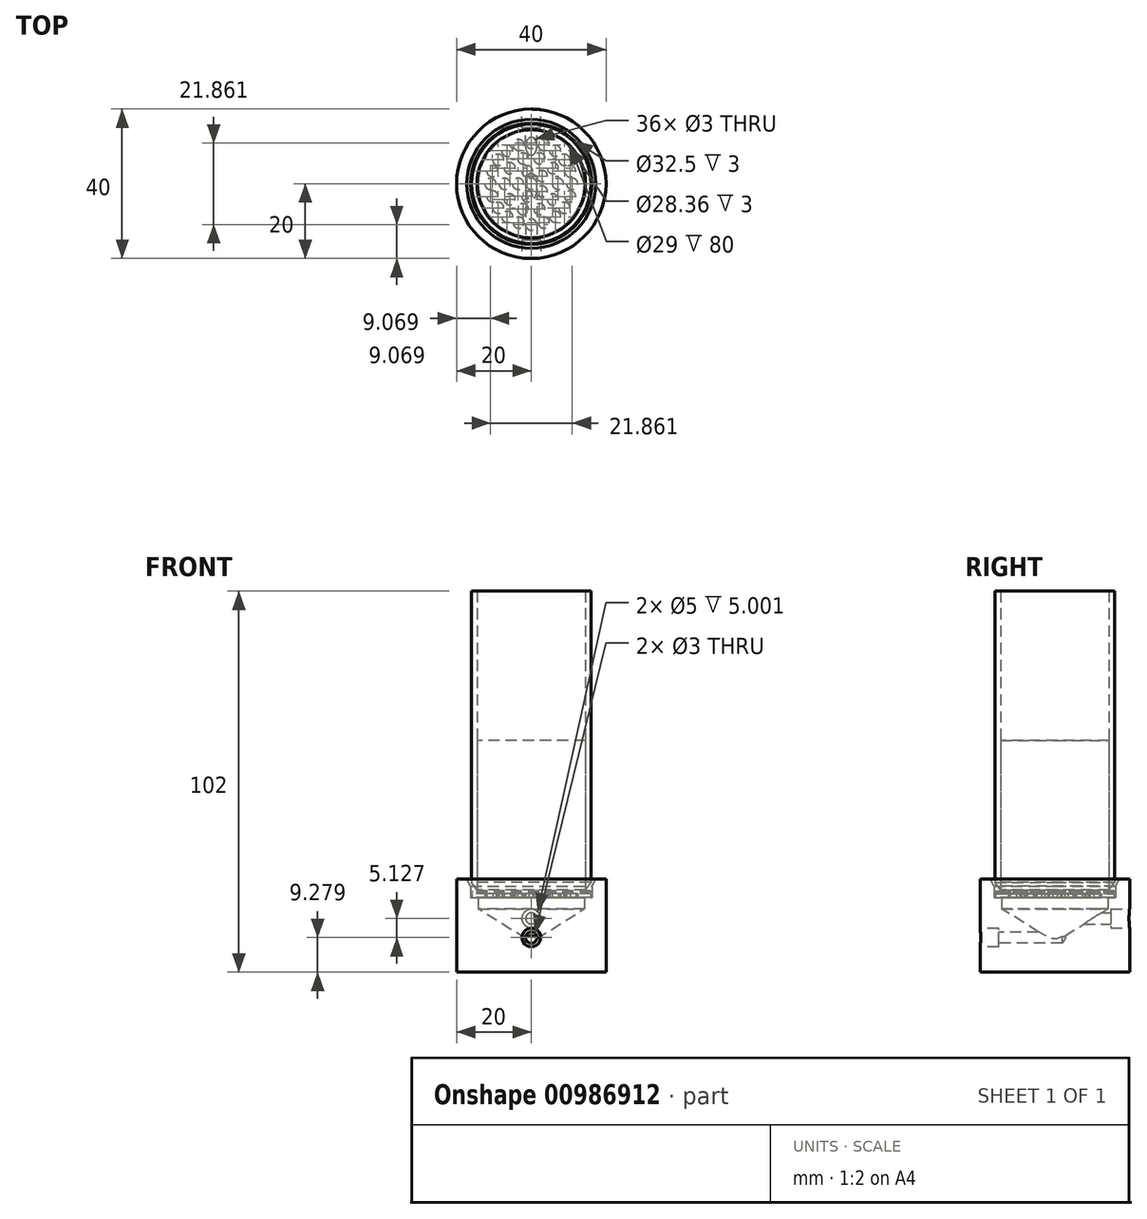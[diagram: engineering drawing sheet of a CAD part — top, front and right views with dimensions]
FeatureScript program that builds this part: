
annotation { "Feature Type Name" : "Feature", "Feature Type Description" : "" }
export const myFeature = defineFeature(function(context is Context, id is Id, definition is map)
    precondition{}
    {
        {
            var Q0;
            Q0=qCreatedBy(makeId("Top.planeOp"),FACE);
            var sketch = newSketch(context, id + "F0", { "sketchPlane" : qUnion([Q0])});
            skCircle(sketch, "E0", {"center": v(0, 0) * mm, "radius": 16 * mm});
            skCircle(sketch, "E1", {"center": v(0, 0) * mm, "radius": 14.5 * mm});
            skSolve(sketch);
        }
        {
            var Q0;
            Q0=makeQuery(id+"F0.imprint","IMPRINT",FACE,{"disambiguationData":[TD([[makeQuery(id+"F0.imprint","IMPRINT",EDGE,{"derivedFrom":sQuery(id+"F0.wireOp",EDGE,"E0")}),1.0]])]});
            extrude(context, id + "F1", {"entities" : qUnion([Q0]), "depth" : 80 * mm, "offsetDistance" : 25 * mm});
        }
        {
            var Q0;
            Q0=qCreatedBy(makeId("Front.planeOp"),FACE);
            var sketch = newSketch(context, id + "F2", { "sketchPlane" : qUnion([Q0])});
            skLineSegment(sketch, "E2", {"start": v(-16.25, 0) * mm, "end": v(-16.25, 5) * mm});
            skLineSegment(sketch, "E3", {"start": v(-16.25, 5) * mm, "end": v(-20, 5) * mm});
            skLineSegment(sketch, "E4", {"start": v(-20, 5) * mm, "end": v(-20, -20) * mm});
            skLineSegment(sketch, "E5", {"start": v(-20, -20) * mm, "end": v(0, -20) * mm});
            skLineSegment(sketch, "E6", {"start": v(0, -20) * mm, "end": v(0, -12) * mm});
            skLineSegment(sketch, "E7", {"start": v(0, -12) * mm, "end": v(-14.18, -3) * mm});
            skLineSegment(sketch, "E8", {"start": v(-14.18, -3) * mm, "end": v(-14.18, 0) * mm});
            skLineSegment(sketch, "E9", {"start": v(-14.18, 0) * mm, "end": v(-16.25, 0) * mm});
            skSolve(sketch);
        }
        {
            var Q0;
            Q0=makeQuery(id+"F2.imprint","IMPRINT",FACE,{"disambiguationData":[TD([[makeQuery(id+"F2.imprint","IMPRINT",EDGE,{"derivedFrom":sQuery(id+"F2.wireOp",EDGE,"E2")}),1.0]])]});
            var Q1;
            Q1=sQuery(id+"F2.wireOp",EDGE,"E6");
            revolve(context, id + "F3", {"surfaceOperationType" : NewSurfaceOperationType.NEW, "entities" : qUnion([Q0]), "axis" : qUnion([Q1]), "revolveType" : RevolveType.FULL});
        }
        {
            var Q0;
            Q0=qCreatedBy(makeId("Front.planeOp"),FACE);
            cPlane(context, id + "F4", {"entities" : qUnion([Q0]), "cplaneType" : CPlaneType.OFFSET, "offset" : 20 * mm, "width" : 150 * mm, "height" : 150 * mm});
        }
        {
            var Q0;
            Q0=qCreatedBy(id+"F4.planeOp",FACE);
            var sketch = newSketch(context, id + "F5", { "sketchPlane" : qUnion([Q0])});
            skLineSegment(sketch, "E10", {"start": v(0, -20.72) * mm, "end": v(0, -10.72) * mm});
            skSolve(sketch);
        }
        {
            var Q0;
            Q0=sQuery(id+"F5.wireOp",VERTEX,"E10.end");
            var Q1;
            Q1=makeQuery(id+"F3.opRevolve","SWEPT_BODY",BODY,{"disambiguationData":[OSD([sQuery(id+"F2.wireOp",EDGE,"E2"),sQuery(id+"F2.wireOp",EDGE,"E3"),sQuery(id+"F2.wireOp",EDGE,"E4"),sQuery(id+"F2.wireOp",EDGE,"E5"),sQuery(id+"F2.wireOp",EDGE,"E6"),sQuery(id+"F2.wireOp",EDGE,"E7"),sQuery(id+"F2.wireOp",EDGE,"E8"),sQuery(id+"F2.wireOp",EDGE,"E9")])]});
            hole(context, id + "F6", {"style" : HoleStyle.C_BORE, "endStyle" : HoleEndStyle.BLIND, "holeDiameter" : 3 * mm, "cBoreDiameter" : 5 * mm, "cBoreDepth" : 5 * mm, "majorDiameter" : 5 * mm, "holeDepth" : 22 * mm, "isTappedThrough" : true, "tappedDepth" : 12 * mm, "tapClearance" : 3, "startFromSketch" : true, "locations" : qUnion([Q0]), "scope" : qUnion([Q1])});
        }
        {
            var Q0;
            Q0=qCreatedBy(makeId("Front.planeOp"),FACE);
            cPlane(context, id + "F7", {"entities" : qUnion([Q0]), "cplaneType" : CPlaneType.OFFSET, "offset" : 20 * mm, "oppositeDirection" : true, "width" : 150 * mm, "height" : 150 * mm});
        }
        {
            var Q0;
            Q0=qCreatedBy(id+"F7.planeOp",FACE);
            var sketch = newSketch(context, id + "F8", { "sketchPlane" : qUnion([Q0])});
            skLineSegment(sketch, "E11", {"start": v(0, -19.77) * mm, "end": v(0, -5.6) * mm});
            skSolve(sketch);
        }
        {
            var Q0;
            Q0=sQuery(id+"F8.wireOp",VERTEX,"E11.end");
            var Q1;
            Q1=makeQuery(id+"F3.opRevolve","SWEPT_BODY",BODY,{"disambiguationData":[OSD([sQuery(id+"F2.wireOp",EDGE,"E2"),sQuery(id+"F2.wireOp",EDGE,"E3"),sQuery(id+"F2.wireOp",EDGE,"E4"),sQuery(id+"F2.wireOp",EDGE,"E5"),sQuery(id+"F2.wireOp",EDGE,"E6"),sQuery(id+"F2.wireOp",EDGE,"E7"),sQuery(id+"F2.wireOp",EDGE,"E8"),sQuery(id+"F2.wireOp",EDGE,"E9")])]});
            hole(context, id + "F9", {"style" : HoleStyle.C_BORE, "endStyle" : HoleEndStyle.BLIND, "oppositeDirection" : true, "holeDiameter" : 3 * mm, "cBoreDiameter" : 5 * mm, "cBoreDepth" : 5 * mm, "majorDiameter" : 5 * mm, "holeDepth" : 22 * mm, "isTappedThrough" : true, "tappedDepth" : 12 * mm, "tapClearance" : 3, "startFromSketch" : true, "locations" : qUnion([Q0]), "scope" : qUnion([Q1])});
        }
        {
            var Q0;
            Q0=makeQuery(id+"F1.opExtrude","SWEPT_BODY",BODY,{"disambiguationData":[OSD([sQuery(id+"F0.wireOp",EDGE,"E0"),sQuery(id+"F0.wireOp",EDGE,"E1")])]});
            transform(context, id + "F10", {"entities" : qUnion([Q0]), "transformType" : TransformType.TRANSLATION_3D, "dx" : 0 * mm, "dy" : 0 * mm, "dz" : 2 * mm, "makeCopy" : false});
        }
        {
            var Q0;
            Q0=qCreatedBy(makeId("Top.planeOp"),FACE);
            var sketch = newSketch(context, id + "F11", { "sketchPlane" : qUnion([Q0])});
            skCircle(sketch, "E12", {"center": v(0, 0) * mm, "radius": 15.9 * mm});
            skSolve(sketch);
        }
        {
            var Q0;
            Q0=makeQuery(id+"F11.imprint","IMPRINT",FACE,{"disambiguationData":[TD([[makeQuery(id+"F11.imprint","IMPRINT",EDGE,{"derivedFrom":sQuery(id+"F11.wireOp",EDGE,"E12")}),1.0]])]});
            extrude(context, id + "F12", {"entities" : qUnion([Q0]), "depth" : 1 * mm, "offsetDistance" : 25 * mm});
        }
        {
            var Q0;
            Q0=qCreatedBy(makeId("Top.planeOp"),FACE);
            var sketch = newSketch(context, id + "F13", { "sketchPlane" : qUnion([Q0])});
            skCircle(sketch, "E13", {"center": v(0, 0) * mm, "radius": 1.5 * mm});
            skCircle(sketch, "E14", {"center": v(-3.54, 0) * mm, "radius": 1.5 * mm});
            skCircle(sketch, "E15.1.0", {"center": v(-1.1, -3.36) * mm, "radius": 1.5 * mm});
            skCircle(sketch, "E15.2.0", {"center": v(2.86, -2.08) * mm, "radius": 1.5 * mm});
            skCircle(sketch, "E15.3.0", {"center": v(2.86, 2.08) * mm, "radius": 1.5 * mm});
            skCircle(sketch, "E15.4.0", {"center": v(-1.1, 3.36) * mm, "radius": 1.5 * mm});
            skCircle(sketch, "E16", {"center": v(-7.13, 0) * mm, "radius": 1.5 * mm});
            skCircle(sketch, "E17.1.0", {"center": v(-5.77, -4.19) * mm, "radius": 1.5 * mm});
            skCircle(sketch, "E17.2.0", {"center": v(-2.2, -6.78) * mm, "radius": 1.5 * mm});
            skCircle(sketch, "E17.3.0", {"center": v(2.2, -6.78) * mm, "radius": 1.5 * mm});
            skCircle(sketch, "E17.4.0", {"center": v(5.77, -4.19) * mm, "radius": 1.5 * mm});
            skCircle(sketch, "E17.5.0", {"center": v(7.13, 0) * mm, "radius": 1.5 * mm});
            skCircle(sketch, "E17.6.0", {"center": v(5.77, 4.19) * mm, "radius": 1.5 * mm});
            skCircle(sketch, "E17.7.0", {"center": v(2.2, 6.78) * mm, "radius": 1.5 * mm});
            skCircle(sketch, "E17.8.0", {"center": v(-2.2, 6.78) * mm, "radius": 1.5 * mm});
            skCircle(sketch, "E17.9.0", {"center": v(-5.77, 4.19) * mm, "radius": 1.5 * mm});
            skCircle(sketch, "E18", {"center": v(-10.93, 0) * mm, "radius": 1.5 * mm});
            skCircle(sketch, "E19.1.0", {"center": v(-10.4, -3.38) * mm, "radius": 1.5 * mm});
            skCircle(sketch, "E19.2.0", {"center": v(-8.84, -6.42) * mm, "radius": 1.5 * mm});
            skCircle(sketch, "E19.3.0", {"center": v(-6.42, -8.84) * mm, "radius": 1.5 * mm});
            skCircle(sketch, "E19.4.0", {"center": v(-3.38, -10.4) * mm, "radius": 1.5 * mm});
            skCircle(sketch, "E19.5.0", {"center": v(0, -10.93) * mm, "radius": 1.5 * mm});
            skCircle(sketch, "E19.6.0", {"center": v(3.38, -10.4) * mm, "radius": 1.5 * mm});
            skCircle(sketch, "E19.7.0", {"center": v(6.42, -8.84) * mm, "radius": 1.5 * mm});
            skCircle(sketch, "E19.8.0", {"center": v(8.84, -6.42) * mm, "radius": 1.5 * mm});
            skCircle(sketch, "E19.9.0", {"center": v(10.4, -3.38) * mm, "radius": 1.5 * mm});
            skCircle(sketch, "E19.10.0", {"center": v(10.93, 0) * mm, "radius": 1.5 * mm});
            skCircle(sketch, "E19.11.0", {"center": v(10.4, 3.38) * mm, "radius": 1.5 * mm});
            skCircle(sketch, "E19.12.0", {"center": v(8.84, 6.42) * mm, "radius": 1.5 * mm});
            skCircle(sketch, "E19.13.0", {"center": v(6.42, 8.84) * mm, "radius": 1.5 * mm});
            skCircle(sketch, "E19.14.0", {"center": v(3.38, 10.4) * mm, "radius": 1.5 * mm});
            skCircle(sketch, "E19.15.0", {"center": v(0, 10.93) * mm, "radius": 1.5 * mm});
            skCircle(sketch, "E19.16.0", {"center": v(-3.38, 10.4) * mm, "radius": 1.5 * mm});
            skCircle(sketch, "E19.17.0", {"center": v(-6.42, 8.84) * mm, "radius": 1.5 * mm});
            skCircle(sketch, "E19.18.0", {"center": v(-8.84, 6.42) * mm, "radius": 1.5 * mm});
            skCircle(sketch, "E19.19.0", {"center": v(-10.4, 3.38) * mm, "radius": 1.5 * mm});
            skSolve(sketch);
        }
        {
            var Q0;
            Q0=makeQuery(id+"F13.imprint","IMPRINT",FACE,{"disambiguationData":[TD([[makeQuery(id+"F13.imprint","IMPRINT",EDGE,{"derivedFrom":sQuery(id+"F13.wireOp",EDGE,"E19.7.0")}),1.0]])]});
            var Q1;
            Q1=makeQuery(id+"F13.imprint","IMPRINT",FACE,{"disambiguationData":[TD([[makeQuery(id+"F13.imprint","IMPRINT",EDGE,{"derivedFrom":sQuery(id+"F13.wireOp",EDGE,"E19.3.0")}),1.0]])]});
            var Q2;
            Q2=makeQuery(id+"F13.imprint","IMPRINT",FACE,{"disambiguationData":[TD([[makeQuery(id+"F13.imprint","IMPRINT",EDGE,{"derivedFrom":sQuery(id+"F13.wireOp",EDGE,"E19.1.0")}),1.0]])]});
            var Q3;
            Q3=makeQuery(id+"F13.imprint","IMPRINT",FACE,{"disambiguationData":[TD([[makeQuery(id+"F13.imprint","IMPRINT",EDGE,{"derivedFrom":sQuery(id+"F13.wireOp",EDGE,"E19.5.0")}),1.0]])]});
            var Q4;
            Q4=makeQuery(id+"F13.imprint","IMPRINT",FACE,{"disambiguationData":[TD([[makeQuery(id+"F13.imprint","IMPRINT",EDGE,{"derivedFrom":sQuery(id+"F13.wireOp",EDGE,"E19.17.0")}),1.0]])]});
            var Q5;
            Q5=makeQuery(id+"F13.imprint","IMPRINT",FACE,{"disambiguationData":[TD([[makeQuery(id+"F13.imprint","IMPRINT",EDGE,{"derivedFrom":sQuery(id+"F13.wireOp",EDGE,"E19.14.0")}),1.0]])]});
            var Q6;
            Q6=makeQuery(id+"F13.imprint","IMPRINT",FACE,{"disambiguationData":[TD([[makeQuery(id+"F13.imprint","IMPRINT",EDGE,{"derivedFrom":sQuery(id+"F13.wireOp",EDGE,"E19.19.0")}),1.0]])]});
            var Q7;
            Q7=makeQuery(id+"F13.imprint","IMPRINT",FACE,{"disambiguationData":[TD([[makeQuery(id+"F13.imprint","IMPRINT",EDGE,{"derivedFrom":sQuery(id+"F13.wireOp",EDGE,"E19.15.0")}),1.0]])]});
            var Q8;
            Q8=makeQuery(id+"F13.imprint","IMPRINT",FACE,{"disambiguationData":[TD([[makeQuery(id+"F13.imprint","IMPRINT",EDGE,{"derivedFrom":sQuery(id+"F13.wireOp",EDGE,"E17.9.0")}),1.0]])]});
            var Q9;
            Q9=makeQuery(id+"F13.imprint","IMPRINT",FACE,{"disambiguationData":[TD([[makeQuery(id+"F13.imprint","IMPRINT",EDGE,{"derivedFrom":sQuery(id+"F13.wireOp",EDGE,"E15.3.0")}),1.0]])]});
            var Q10;
            Q10=makeQuery(id+"F13.imprint","IMPRINT",FACE,{"disambiguationData":[TD([[makeQuery(id+"F13.imprint","IMPRINT",EDGE,{"derivedFrom":sQuery(id+"F13.wireOp",EDGE,"E17.1.0")}),1.0]])]});
            var Q11;
            Q11=makeQuery(id+"F13.imprint","IMPRINT",FACE,{"disambiguationData":[TD([[makeQuery(id+"F13.imprint","IMPRINT",EDGE,{"derivedFrom":sQuery(id+"F13.wireOp",EDGE,"E19.16.0")}),1.0]])]});
            var Q12;
            Q12=makeQuery(id+"F13.imprint","IMPRINT",FACE,{"disambiguationData":[TD([[makeQuery(id+"F13.imprint","IMPRINT",EDGE,{"derivedFrom":sQuery(id+"F13.wireOp",EDGE,"E19.8.0")}),1.0]])]});
            var Q13;
            Q13=makeQuery(id+"F13.imprint","IMPRINT",FACE,{"disambiguationData":[TD([[makeQuery(id+"F13.imprint","IMPRINT",EDGE,{"derivedFrom":sQuery(id+"F13.wireOp",EDGE,"E14")}),1.0]])]});
            var Q14;
            Q14=makeQuery(id+"F13.imprint","IMPRINT",FACE,{"disambiguationData":[TD([[makeQuery(id+"F13.imprint","IMPRINT",EDGE,{"derivedFrom":sQuery(id+"F13.wireOp",EDGE,"E17.2.0")}),1.0]])]});
            var Q15;
            Q15=makeQuery(id+"F13.imprint","IMPRINT",FACE,{"disambiguationData":[TD([[makeQuery(id+"F13.imprint","IMPRINT",EDGE,{"derivedFrom":sQuery(id+"F13.wireOp",EDGE,"E17.8.0")}),1.0]])]});
            var Q16;
            Q16=makeQuery(id+"F13.imprint","IMPRINT",FACE,{"disambiguationData":[TD([[makeQuery(id+"F13.imprint","IMPRINT",EDGE,{"derivedFrom":sQuery(id+"F13.wireOp",EDGE,"E19.12.0")}),1.0]])]});
            var Q17;
            Q17=makeQuery(id+"F13.imprint","IMPRINT",FACE,{"disambiguationData":[TD([[makeQuery(id+"F13.imprint","IMPRINT",EDGE,{"derivedFrom":sQuery(id+"F13.wireOp",EDGE,"E17.7.0")}),1.0]])]});
            var Q18;
            Q18=makeQuery(id+"F13.imprint","IMPRINT",FACE,{"disambiguationData":[TD([[makeQuery(id+"F13.imprint","IMPRINT",EDGE,{"derivedFrom":sQuery(id+"F13.wireOp",EDGE,"E19.13.0")}),1.0]])]});
            var Q19;
            Q19=makeQuery(id+"F13.imprint","IMPRINT",FACE,{"disambiguationData":[TD([[makeQuery(id+"F13.imprint","IMPRINT",EDGE,{"derivedFrom":sQuery(id+"F13.wireOp",EDGE,"E13")}),1.0]])]});
            var Q20;
            Q20=makeQuery(id+"F13.imprint","IMPRINT",FACE,{"disambiguationData":[TD([[makeQuery(id+"F13.imprint","IMPRINT",EDGE,{"derivedFrom":sQuery(id+"F13.wireOp",EDGE,"E19.9.0")}),1.0]])]});
            var Q21;
            Q21=makeQuery(id+"F13.imprint","IMPRINT",FACE,{"disambiguationData":[TD([[makeQuery(id+"F13.imprint","IMPRINT",EDGE,{"derivedFrom":sQuery(id+"F13.wireOp",EDGE,"E19.10.0")}),1.0]])]});
            var Q22;
            Q22=makeQuery(id+"F13.imprint","IMPRINT",FACE,{"disambiguationData":[TD([[makeQuery(id+"F13.imprint","IMPRINT",EDGE,{"derivedFrom":sQuery(id+"F13.wireOp",EDGE,"E17.6.0")}),1.0]])]});
            var Q23;
            Q23=makeQuery(id+"F13.imprint","IMPRINT",FACE,{"disambiguationData":[TD([[makeQuery(id+"F13.imprint","IMPRINT",EDGE,{"derivedFrom":sQuery(id+"F13.wireOp",EDGE,"E17.4.0")}),1.0]])]});
            var Q24;
            Q24=makeQuery(id+"F13.imprint","IMPRINT",FACE,{"disambiguationData":[TD([[makeQuery(id+"F13.imprint","IMPRINT",EDGE,{"derivedFrom":sQuery(id+"F13.wireOp",EDGE,"E19.11.0")}),1.0]])]});
            var Q25;
            Q25=makeQuery(id+"F13.imprint","IMPRINT",FACE,{"disambiguationData":[TD([[makeQuery(id+"F13.imprint","IMPRINT",EDGE,{"derivedFrom":sQuery(id+"F13.wireOp",EDGE,"E17.3.0")}),1.0]])]});
            var Q26;
            Q26=makeQuery(id+"F13.imprint","IMPRINT",FACE,{"disambiguationData":[TD([[makeQuery(id+"F13.imprint","IMPRINT",EDGE,{"derivedFrom":sQuery(id+"F13.wireOp",EDGE,"E16")}),1.0]])]});
            var Q27;
            Q27=makeQuery(id+"F13.imprint","IMPRINT",FACE,{"disambiguationData":[TD([[makeQuery(id+"F13.imprint","IMPRINT",EDGE,{"derivedFrom":sQuery(id+"F13.wireOp",EDGE,"E15.1.0")}),1.0]])]});
            var Q28;
            Q28=makeQuery(id+"F13.imprint","IMPRINT",FACE,{"disambiguationData":[TD([[makeQuery(id+"F13.imprint","IMPRINT",EDGE,{"derivedFrom":sQuery(id+"F13.wireOp",EDGE,"E19.6.0")}),1.0]])]});
            var Q29;
            Q29=makeQuery(id+"F13.imprint","IMPRINT",FACE,{"disambiguationData":[TD([[makeQuery(id+"F13.imprint","IMPRINT",EDGE,{"derivedFrom":sQuery(id+"F13.wireOp",EDGE,"E15.2.0")}),1.0]])]});
            var Q30;
            Q30=makeQuery(id+"F13.imprint","IMPRINT",FACE,{"disambiguationData":[TD([[makeQuery(id+"F13.imprint","IMPRINT",EDGE,{"derivedFrom":sQuery(id+"F13.wireOp",EDGE,"E15.4.0")}),1.0]])]});
            var Q31;
            Q31=makeQuery(id+"F13.imprint","IMPRINT",FACE,{"disambiguationData":[TD([[makeQuery(id+"F13.imprint","IMPRINT",EDGE,{"derivedFrom":sQuery(id+"F13.wireOp",EDGE,"E19.4.0")}),1.0]])]});
            var Q32;
            Q32=makeQuery(id+"F13.imprint","IMPRINT",FACE,{"disambiguationData":[TD([[makeQuery(id+"F13.imprint","IMPRINT",EDGE,{"derivedFrom":sQuery(id+"F13.wireOp",EDGE,"E19.2.0")}),1.0]])]});
            var Q33;
            Q33=makeQuery(id+"F13.imprint","IMPRINT",FACE,{"disambiguationData":[TD([[makeQuery(id+"F13.imprint","IMPRINT",EDGE,{"derivedFrom":sQuery(id+"F13.wireOp",EDGE,"E18")}),1.0]])]});
            var Q34;
            Q34=makeQuery(id+"F13.imprint","IMPRINT",FACE,{"disambiguationData":[TD([[makeQuery(id+"F13.imprint","IMPRINT",EDGE,{"derivedFrom":sQuery(id+"F13.wireOp",EDGE,"E19.18.0")}),1.0]])]});
            var Q35;
            Q35=makeQuery(id+"F13.imprint","IMPRINT",FACE,{"disambiguationData":[TD([[makeQuery(id+"F13.imprint","IMPRINT",EDGE,{"derivedFrom":sQuery(id+"F13.wireOp",EDGE,"E17.5.0")}),1.0]])]});
            extrude(context, id + "F14", {"entities" : qUnion([Q0, Q1, Q2, Q3, Q4, Q5, Q6, Q7, Q8, Q9, Q10, Q11, Q12, Q13, Q14, Q15, Q16, Q17, Q18, Q19, Q20, Q21, Q22, Q23, Q24, Q25, Q26, Q27, Q28, Q29, Q30, Q31, Q32, Q33, Q34, Q35]), "operationType" : NewBodyOperationType.REMOVE, "depth" : 1 * mm, "offsetDistance" : 25 * mm});
        }
        {
            var Q0;
            Q0=qCreatedBy(makeId("Top.planeOp"),FACE);
            var sketch = newSketch(context, id + "F15", { "sketchPlane" : qUnion([Q0])});
            skCircle(sketch, "E20", {"center": v(0, 0) * mm, "radius": 14.5 * mm});
            skSolve(sketch);
        }
        {
            var Q0;
            Q0=makeQuery(id+"F15.imprint","IMPRINT",FACE,{"disambiguationData":[TD([[makeQuery(id+"F15.imprint","IMPRINT",EDGE,{"derivedFrom":sQuery(id+"F15.wireOp",EDGE,"E20")}),1.0]])]});
            extrude(context, id + "F16", {"entities" : qUnion([Q0]), "depth" : 40 * mm, "offsetDistance" : 25 * mm});
        }
        {
            var Q0;
            Q0=makeQuery(id+"F16.opExtrude","SWEPT_BODY",BODY,{"disambiguationData":[OSD([sQuery(id+"F15.wireOp",EDGE,"E20")])]});
            transform(context, id + "F17", {"entities" : qUnion([Q0]), "transformType" : TransformType.TRANSLATION_3D, "dx" : 0 * mm, "dy" : 0 * mm, "dz" : 2 * mm, "makeCopy" : false});
        }
        {
            var Q0;
            Q0=qCreatedBy(makeId("Top.planeOp"),FACE);
            var sketch = newSketch(context, id + "F18", { "sketchPlane" : qUnion([Q0])});
            skCircle(sketch, "E21", {"center": v(0, 0) * mm, "radius": 15.9 * mm});
            skSolve(sketch);
        }
        {
            var Q0;
            Q0=makeQuery(id+"F18.imprint","IMPRINT",FACE,{"disambiguationData":[TD([[makeQuery(id+"F18.imprint","IMPRINT",EDGE,{"derivedFrom":sQuery(id+"F18.wireOp",EDGE,"E21")}),1.0]])]});
            extrude(context, id + "F19", {"entities" : qUnion([Q0]), "depth" : 0.5 * mm, "offsetDistance" : 25 * mm});
        }
        {
            var Q0;
            Q0=makeQuery(id+"F19.opExtrude","SWEPT_BODY",BODY,{"disambiguationData":[OSD([sQuery(id+"F18.wireOp",EDGE,"E21")])]});
            transform(context, id + "F20", {"entities" : qUnion([Q0]), "transformType" : TransformType.TRANSLATION_3D, "dx" : 0 * mm, "dy" : 0 * mm, "dz" : 1.25 * mm, "makeCopy" : false});
        }
        {
            var Q0;
            Q0=makeQuery(id+"F3.opRevolve","SWEPT_EDGE",EDGE,{"disambiguationData":[OSD([sQuery(id+"F2.wireOp",EDGE,"E2"),sQuery(id+"F2.wireOp",EDGE,"E3")])]});
            chamfer(context, id + "F21", {"entities" : qUnion([Q0]), "chamferType" : ChamferType.TWO_OFFSETS, "width1" : 1 * mm, "oppositeDirection" : false, "width2" : 2 * mm, "tangentPropagation" : true});
        }
        {
            var Q0;
            Q0=makeQuery(id+"F1.opExtrude","CAP_EDGE",EDGE,{"disambiguationData":[OSD([sQuery(id+"F0.wireOp",EDGE,"E0")])],"isStart":true});
            chamfer(context, id + "F22", {"entities" : qUnion([Q0]), "chamferType" : ChamferType.TWO_OFFSETS, "width1" : 2 * mm, "oppositeDirection" : false, "width2" : 1.5 * mm, "tangentPropagation" : true});
        }
        {
            var Q0;
            Q0=makeQuery(id+"F3.opRevolve","SWEPT_BODY",BODY,{"disambiguationData":[OSD([sQuery(id+"F2.wireOp",EDGE,"E2"),sQuery(id+"F2.wireOp",EDGE,"E3"),sQuery(id+"F2.wireOp",EDGE,"E4"),sQuery(id+"F2.wireOp",EDGE,"E5"),sQuery(id+"F2.wireOp",EDGE,"E6"),sQuery(id+"F2.wireOp",EDGE,"E7"),sQuery(id+"F2.wireOp",EDGE,"E8"),sQuery(id+"F2.wireOp",EDGE,"E9")])]});
            transform(context, id + "F23", {"entities" : qUnion([Q0]), "transformType" : TransformType.TRANSLATION_3D, "dx" : 0 * mm, "dy" : 0 * mm, "dz" : 0 * mm, "makeCopy" : true});
        }
        {
            var Q0;
            Q0=makeQuery(id+"F3.opRevolve","SWEPT_BODY",BODY,{"disambiguationData":[OSD([sQuery(id+"F2.wireOp",EDGE,"E2"),sQuery(id+"F2.wireOp",EDGE,"E3"),sQuery(id+"F2.wireOp",EDGE,"E4"),sQuery(id+"F2.wireOp",EDGE,"E5"),sQuery(id+"F2.wireOp",EDGE,"E6"),sQuery(id+"F2.wireOp",EDGE,"E7"),sQuery(id+"F2.wireOp",EDGE,"E8"),sQuery(id+"F2.wireOp",EDGE,"E9")])]});
            deleteBodies(context, id + "F24", {"entities" : qUnion([Q0])});
        }
    });
